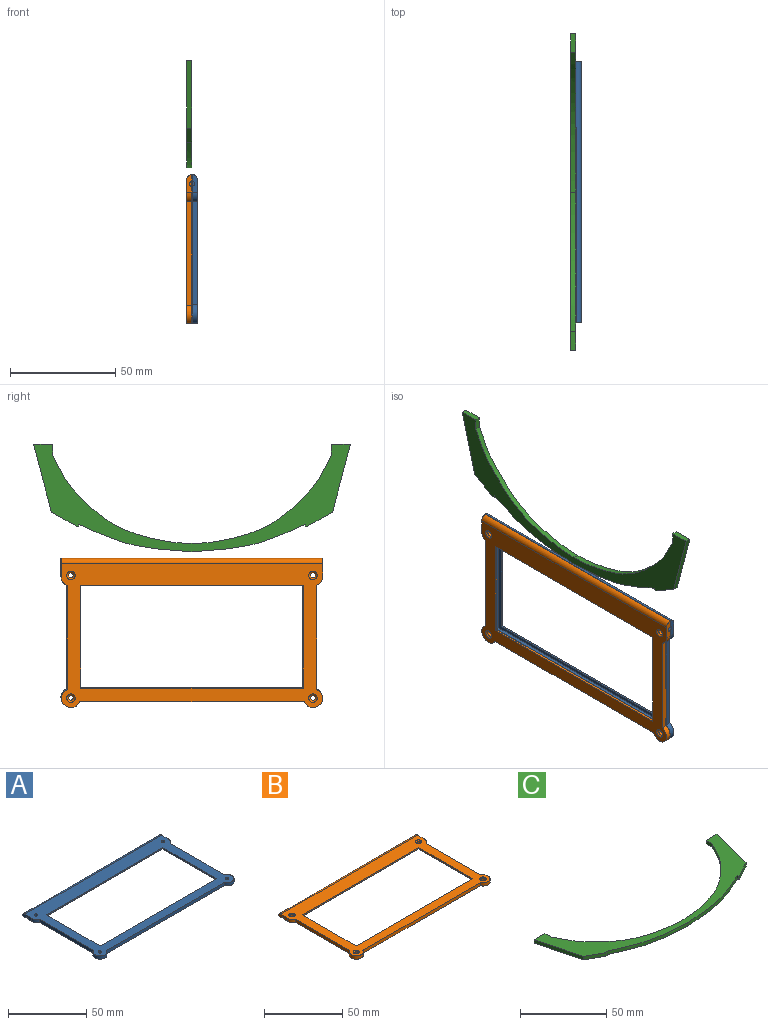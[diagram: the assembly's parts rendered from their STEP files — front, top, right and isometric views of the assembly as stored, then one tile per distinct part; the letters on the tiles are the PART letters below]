
ASSEMBLY  parts=3 mates=3
PART A: 29 faces, bbox 124.1x70.6x2.5 mm
  f0: plane 124.05x70.61mm, normal (0,0,-1), area 2503.8mm2, adj f1,f5,f6,f7,f8,f9,f10,f11
  f1: plane 8.38x2.5mm, normal (1,0,0), area 17.2mm2, adj f0,f5,f18,f24,f28
  f2: plane 48.75x1mm, normal (1,0,0), area 48.8mm2, adj f3,f15,f18,f23
  f3: plane 105.5x1mm, normal (0,-1,0), area 105.5mm2, adj f2,f4,f18,f23
  f4: plane 48.75x1mm, normal (-1,0,0), area 48.8mm2, adj f3,f15,f18,f23
  f5: cylinder r=4.5mm len=4.45mm, axis (0,0,-1), area 14mm2, adj f0,f1,f16,f18
  f6: plane 8.73x2.5mm, normal (-1,0,0), area 18mm2, adj f0,f7,f18,f26,f28
  f7: cylinder r=4.5mm len=4.11mm, axis (0,0,-1), area 13.1mm2, adj f0,f6,f8,f18
  f8: plane 49.12x2.5mm, normal (-1,0,0), area 122.8mm2, adj f0,f7,f9,f18
  f9: cylinder r=4.5mm len=8.66mm, axis (0,0,-1), area 43.6mm2, adj f0,f8,f10,f18
  f10: plane 106.9x2.5mm, normal (0,-1,0), area 267.2mm2, adj f0,f9,f11,f18
  f11: cylinder r=4.5mm len=8.66mm, axis (0,0,-1), area 43.6mm2, adj f0,f10,f16,f18
  f12: cylinder r=1.25mm len=2.5mm, axis (0,0,-1), area 19.6mm2, adj f0,f18
  f13: cylinder r=1.25mm len=2.5mm, axis (0,0,-1), area 19.6mm2, adj f0,f18
  f14: cylinder r=1.25mm len=2.5mm, axis (0,0,-1), area 19.6mm2, adj f0,f18
  f15: plane 105.5x1mm, normal (0,1,0), area 105.5mm2, adj f2,f4,f18,f23
  f16: plane 49.12x2.5mm, normal (1,0,0), area 122.8mm2, adj f0,f5,f11,f18
  f17: cylinder r=1.25mm len=2.5mm, axis (0,0,-1), area 19.6mm2, adj f0,f18
  f18: plane 124.05x68.11mm, normal (0,0,1), area 2709.5mm2, adj f1,f2,f3,f4,f5,f6,f7,f8
  f19: plane 108.5x1.5mm, normal (0,-1,0), area 162.7mm2, adj f0,f20,f22,f23
  f20: plane 51.75x1.5mm, normal (1,0,0), area 77.6mm2, adj f0,f19,f21,f23
  f21: plane 108.5x1.5mm, normal (0,1,0), area 162.7mm2, adj f0,f20,f22,f23
  f22: plane 51.75x1.5mm, normal (-1,0,0), area 77.6mm2, adj f0,f19,f21,f23
  f23: plane 108.5x51.75mm, normal (0,0,-1), area 471.8mm2, adj f2,f3,f4,f15,f19,f20,f21,f22
  f24: cylinder r=1.25mm len=8.8mm, axis (1,0,0), area 34.6mm2, adj f0,f1,f25
  f25: plane 2.5x1.25mm, normal (1,0,0), area 2.5mm2, adj f0,f24
  f26: cylinder r=1.25mm len=8.8mm, axis (-1,0,0), area 34.6mm2, adj f0,f6,f27
  f27: plane 2.5x1.25mm, normal (-1,0,0), area 2.5mm2, adj f0,f26
  f28: cylinder r=2.5mm len=124.04mm, axis (1,0,0), area 487.1mm2, adj f0,f1,f6,f18
PART B: 33 faces, bbox 124.1x70.7x2.5 mm
  f0: plane 124.05x70.75mm, normal (0,0,-1), area 2503.8mm2, adj f1,f5,f6,f7,f8,f9,f10,f11
  f1: plane 8.38x2.5mm, normal (1,0,0), area 17.2mm2, adj f0,f5,f18,f24,f28
  f2: plane 48.75x1mm, normal (1,0,0), area 48.8mm2, adj f3,f15,f18,f23
  f3: plane 105.5x1mm, normal (0,-1,0), area 105.5mm2, adj f2,f4,f18,f23
  f4: plane 48.75x1mm, normal (-1,0,0), area 48.8mm2, adj f3,f15,f18,f23
  f5: cylinder r=4.5mm len=4.45mm, axis (0,0,-1), area 14mm2, adj f0,f1,f16,f18
  f6: plane 8.73x2.5mm, normal (-1,0,0), area 18mm2, adj f0,f7,f18,f26,f28
  f7: cylinder r=4.5mm len=4.11mm, axis (0,0,-1), area 13.1mm2, adj f0,f6,f8,f18
  f8: plane 49.32x2.5mm, normal (-1,0,0), area 123.3mm2, adj f0,f7,f9,f18
  f9: cylinder r=4.5mm len=8.64mm, axis (0,0,-1), area 43.7mm2, adj f0,f8,f10,f18
  f10: plane 106.5x2.5mm, normal (0,-1,0), area 266.2mm2, adj f0,f9,f11,f18
  f11: cylinder r=4.5mm len=8.64mm, axis (0,0,-1), area 43.7mm2, adj f0,f10,f16,f18
  f12: cylinder r=1.25mm len=2.5mm, axis (0,0,-1), area 13.7mm2, adj f0,f29
  f13: cylinder r=1.25mm len=2.5mm, axis (0,0,-1), area 13.7mm2, adj f0,f30
  f14: cylinder r=1.25mm len=2.5mm, axis (0,0,-1), area 13.7mm2, adj f0,f31
  f15: plane 105.5x1mm, normal (0,1,0), area 105.5mm2, adj f2,f4,f18,f23
  f16: plane 49.32x2.5mm, normal (1,0,0), area 123.3mm2, adj f0,f5,f11,f18
  f17: cylinder r=1.25mm len=2.5mm, axis (0,0,-1), area 13.7mm2, adj f0,f32
  f18: plane 124.05x68.25mm, normal (0,0,1), area 2678.8mm2, adj f1,f2,f3,f4,f5,f6,f7,f8
  f19: plane 108.5x1.5mm, normal (0,-1,0), area 162.7mm2, adj f0,f20,f22,f23
  f20: plane 51.75x1.5mm, normal (1,0,0), area 77.6mm2, adj f0,f19,f21,f23
  f21: plane 108.5x1.5mm, normal (0,1,0), area 162.7mm2, adj f0,f20,f22,f23
  f22: plane 51.75x1.5mm, normal (-1,0,0), area 77.6mm2, adj f0,f19,f21,f23
  f23: plane 108.5x51.75mm, normal (0,0,-1), area 471.8mm2, adj f2,f3,f4,f15,f19,f20,f21,f22
  f24: cylinder r=1.25mm len=8.8mm, axis (1,0,0), area 34.6mm2, adj f0,f1,f25
  f25: plane 2.5x1.25mm, normal (1,0,0), area 2.5mm2, adj f0,f24
  f26: cylinder r=1.25mm len=8.8mm, axis (-1,0,0), area 34.6mm2, adj f0,f6,f27
  f27: plane 2.5x1.25mm, normal (-1,0,0), area 2.5mm2, adj f0,f26
  f28: cylinder r=2.5mm len=124.04mm, axis (1,0,0), area 487.1mm2, adj f0,f1,f6,f18
  f29: cone r=2mm half-angle=45deg, axis (0,0,1), area 10.8mm2, adj f12,f18
  f30: cone r=1.25mm half-angle=45deg, axis (0,0,1), area 10.8mm2, adj f13,f18
  f31: cone r=2mm half-angle=45deg, axis (0,0,1), area 10.8mm2, adj f14,f18
  f32: cone r=1.25mm half-angle=45deg, axis (0,0,1), area 10.8mm2, adj f17,f18
PART C: 18 faces, bbox 150.2x51x2.5 mm
  f0: plane 9x2.45mm, normal (0,1,0), area 22mm2, adj f1,f7,f8,f9
  f1: plane 5.15x2.45mm, normal (-1,0,0), area 12.6mm2, adj f0,f2,f8,f9
  f2: extruded ~66.1x41.8mm, area 203.4mm2, adj f1,f8,f9,f12
  f3: extruded ~53.74x13.12mm, area 136.8mm2, adj f4,f8,f9,f13
  f4: plane 2.45x0.89mm, normal (-1,0,0), area 2.2mm2, adj f3,f5,f8,f9
  f5: plane 2.45x1.13mm, normal (0,-1,0), area 2.8mm2, adj f4,f6,f8,f9
  f6: plane 11.79x6.53mm, normal (0.48,-0.87,0), area 33mm2, adj f5,f7,f8,f9
  f7: plane 32.18x8.45mm, normal (0.97,-0.25,0), area 81.5mm2, adj f0,f6,f8,f9
  f8: plane 150.2x50.95mm, normal (0,0,1), area 1489.3mm2, adj f0,f1,f2,f3,f4,f5,f6,f7
  f9: plane 150.2x50.95mm, normal (0,0,-1), area 1489.3mm2, adj f0,f1,f2,f3,f4,f5,f6,f7
  f10: plane 9x2.45mm, normal (0,1,0), area 22mm2, adj f8,f9,f11,f17
  f11: plane 5.15x2.45mm, normal (1,0,0), area 12.6mm2, adj f8,f9,f10,f12
  f12: extruded ~66.1x41.8mm, area 203.4mm2, adj f2,f8,f9,f11
  f13: extruded ~53.74x13.12mm, area 136.8mm2, adj f3,f8,f9,f14
  f14: plane 2.45x0.89mm, normal (1,0,0), area 2.2mm2, adj f8,f9,f13,f15
  f15: plane 2.45x1.13mm, normal (0,-1,0), area 2.8mm2, adj f8,f9,f14,f16
  f16: plane 11.79x6.53mm, normal (-0.48,-0.87,0), area 33mm2, adj f8,f9,f15,f17
  f17: plane 32.18x8.45mm, normal (-0.97,-0.25,0), area 81.5mm2, adj f8,f9,f10,f16
PLACE A rot(axis=(0.58,0.58,0.58),120deg) t=(0,0.14,-40.14)mm
PLACE B rot(axis=(0.58,-0.58,-0.58),120deg) t=(0,0,-40.28)mm
PLACE C rot(axis=(0.58,0.58,0.58),120deg) t=(-2.45,0,50.95)mm
MATE cylindrical A.f17 <-> B.f12  axis (1,0,0) through (2.5,-57.39,-11.17)mm
MATE planar A.f12 <-> B.f17  axis (-1,0,0) through (0,57.66,-11.17)mm
MATE planar C.f8 <-> B.f12  axis (1,0,0) through (0,0,0)mm
